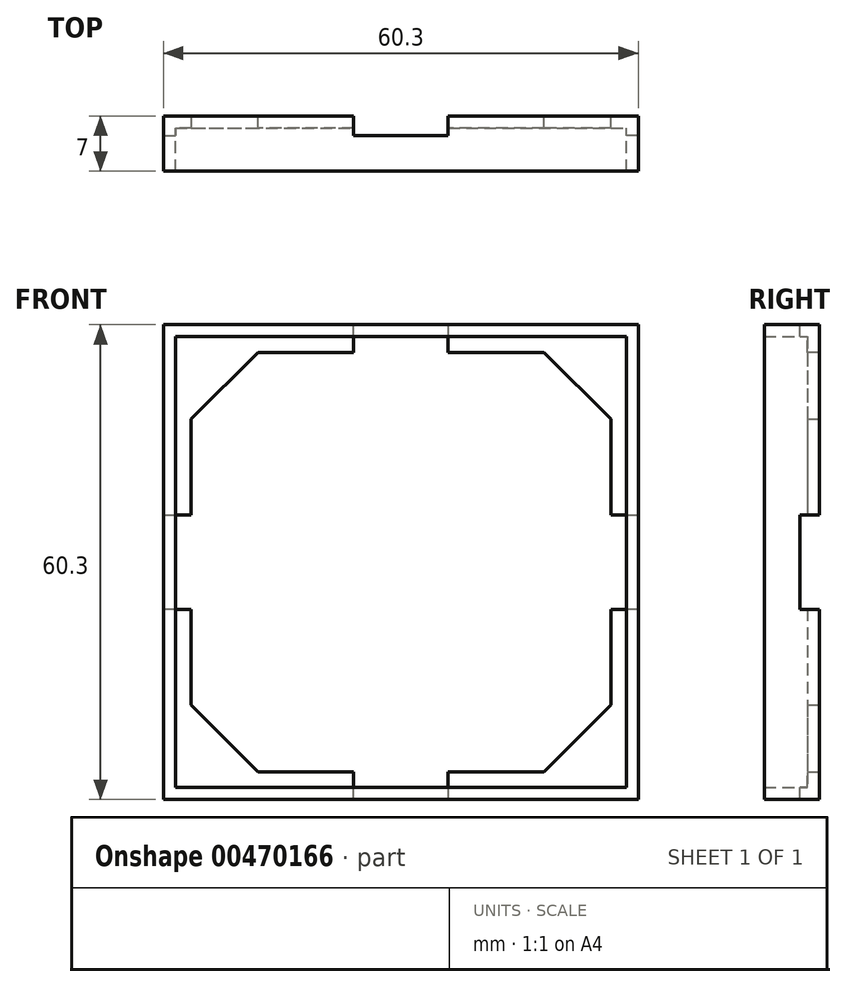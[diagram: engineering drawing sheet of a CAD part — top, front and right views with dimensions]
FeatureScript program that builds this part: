
annotation { "Feature Type Name" : "Feature", "Feature Type Description" : "" }
export const myFeature = defineFeature(function(context is Context, id is Id, definition is map)
    precondition{}
    {
        {
            var Q0;
            Q0=qCreatedBy(makeId("Front.planeOp"),FACE);
            var sketch = newSketch(context, id + "F0", { "sketchPlane" : qUnion([Q0])});
            skLineSegment(sketch, "E0.bottom", {"start": v(-28.65, 28.65) * mm, "end": v(28.65, 28.65) * mm});
            skLineSegment(sketch, "E0.top", {"start": v(-28.65, -28.65) * mm, "end": v(28.65, -28.65) * mm});
            skLineSegment(sketch, "E0.left", {"start": v(-28.65, 28.65) * mm, "end": v(-28.65, -28.65) * mm});
            skLineSegment(sketch, "E0.right", {"start": v(28.65, 28.65) * mm, "end": v(28.65, -28.65) * mm});
            skLineSegment(sketch, "E1", {"start": v(28.65, 28.65) * mm, "end": v(-28.65, -28.65) * mm, "construction": true});
            skLineSegment(sketch, "E2.bottom", {"start": v(18.16, 26.65) * mm, "end": v(-18.16, 26.65) * mm});
            skLineSegment(sketch, "E2.top", {"start": v(18.16, -26.65) * mm, "end": v(-18.16, -26.65) * mm});
            skLineSegment(sketch, "E2.left", {"start": v(26.65, 18.16) * mm, "end": v(26.65, -18.16) * mm});
            skLineSegment(sketch, "E2.right", {"start": v(-26.65, 18.16) * mm, "end": v(-26.65, -18.16) * mm});
            skLineSegment(sketch, "E3", {"start": v(18.16, 26.65) * mm, "end": v(26.65, 18.16) * mm});
            skPoint(sketch, "E4.orphan", {"position": v(26.65, 26.65) * mm});
            skLineSegment(sketch, "E5.1.0", {"start": v(-26.65, 18.16) * mm, "end": v(-18.16, 26.65) * mm});
            skLineSegment(sketch, "E5.2.0", {"start": v(-18.16, -26.65) * mm, "end": v(-26.65, -18.16) * mm});
            skLineSegment(sketch, "E5.3.0", {"start": v(26.65, -18.16) * mm, "end": v(18.16, -26.65) * mm});
            skPoint(sketch, "E5.center", {"position": v(0, 0) * mm});
            skSolve(sketch);
        }
        {
            var Q0;
            Q0=qSketchRegion(id+"F0",true);
            extrude(context, id + "F1", {"entities" : qUnion([Q0]), "depth" : 1.5 * mm});
        }
        {
            var Q0;
            Q0=qCreatedBy(makeId("Front.planeOp"),FACE);
            var sketch = newSketch(context, id + "F2", { "sketchPlane" : qUnion([Q0])});
            skLineSegment(sketch, "E6.0", {"start": v(-28.65, 30.15) * mm, "end": v(28.65, 30.15) * mm});
            skLineSegment(sketch, "E7.0", {"start": v(30.15, 28.65) * mm, "end": v(30.15, -28.65) * mm});
            skLineSegment(sketch, "E8.0", {"start": v(-28.65, -30.15) * mm, "end": v(28.65, -30.15) * mm});
            skLineSegment(sketch, "E9.0", {"start": v(-30.15, 28.65) * mm, "end": v(-30.15, -28.65) * mm});
            skLineSegment(sketch, "E10", {"start": v(-28.65, 30.15) * mm, "end": v(-30.15, 30.15) * mm});
            skLineSegment(sketch, "E11", {"start": v(-30.15, 30.15) * mm, "end": v(-30.15, 28.65) * mm});
            skLineSegment(sketch, "E12", {"start": v(-30.15, -28.65) * mm, "end": v(-30.15, -30.15) * mm});
            skLineSegment(sketch, "E13", {"start": v(-30.15, -30.15) * mm, "end": v(-28.65, -30.15) * mm});
            skLineSegment(sketch, "E14", {"start": v(30.15, -28.65) * mm, "end": v(30.15, -30.15) * mm});
            skLineSegment(sketch, "E15", {"start": v(30.15, -30.15) * mm, "end": v(28.65, -30.15) * mm});
            skLineSegment(sketch, "E16", {"start": v(28.65, 30.15) * mm, "end": v(30.15, 30.15) * mm});
            skPoint(sketch, "E16.endSnap0", {"position": v(30.15, 0) * mm});
            skLineSegment(sketch, "E17", {"start": v(30.15, 30.15) * mm, "end": v(30.15, 28.65) * mm});
            skLineSegment(sketch, "E18.0", {"start": v(-28.65, 28.65) * mm, "end": v(28.65, 28.65) * mm});
            skLineSegment(sketch, "E19.0", {"start": v(-28.65, 28.65) * mm, "end": v(-28.65, -28.65) * mm});
            skLineSegment(sketch, "E20.0", {"start": v(-28.65, -28.65) * mm, "end": v(28.65, -28.65) * mm});
            skLineSegment(sketch, "E21.0", {"start": v(28.65, 28.65) * mm, "end": v(28.65, -28.65) * mm});
            skSolve(sketch);
        }
        {
            var Q0;
            Q0=qSketchRegion(id+"F2",true);
            extrude(context, id + "F3", {"entities" : qUnion([Q0]), "operationType" : NewBodyOperationType.ADD, "depth" : 7 * mm});
        }
        {
            var Q0;
            Q0=qCreatedBy(makeId("Front.planeOp"),FACE);
            var sketch = newSketch(context, id + "F4", { "sketchPlane" : qUnion([Q0])});
            skLineSegment(sketch, "E22", {"start": v(25.58, 0) * mm, "end": v(25.58, 6) * mm});
            skLineSegment(sketch, "E23", {"start": v(25.58, 6) * mm, "end": v(33.95, 6) * mm});
            skLineSegment(sketch, "E24", {"start": v(33.95, 6) * mm, "end": v(33.95, -6) * mm});
            skLineSegment(sketch, "E25", {"start": v(33.95, -6) * mm, "end": v(25.58, -6) * mm});
            skLineSegment(sketch, "E26", {"start": v(25.58, -6) * mm, "end": v(25.58, 0) * mm});
            skLineSegment(sketch, "E27.1.0", {"start": v(-6, 25.58) * mm, "end": v(-6, 33.95) * mm});
            skLineSegment(sketch, "E27.1.1", {"start": v(-6, 33.95) * mm, "end": v(6, 33.95) * mm});
            skLineSegment(sketch, "E27.1.2", {"start": v(6, 25.58) * mm, "end": v(0, 25.58) * mm});
            skLineSegment(sketch, "E27.1.3", {"start": v(0, 25.58) * mm, "end": v(-6, 25.58) * mm});
            skLineSegment(sketch, "E27.1.4", {"start": v(6, 33.95) * mm, "end": v(6, 25.58) * mm});
            skLineSegment(sketch, "E27.2.0", {"start": v(-25.58, -6) * mm, "end": v(-33.95, -6) * mm});
            skLineSegment(sketch, "E27.2.1", {"start": v(-33.95, -6) * mm, "end": v(-33.95, 6) * mm});
            skLineSegment(sketch, "E27.2.2", {"start": v(-25.58, 6) * mm, "end": v(-25.58, 0) * mm});
            skLineSegment(sketch, "E27.2.3", {"start": v(-25.58, 0) * mm, "end": v(-25.58, -6) * mm});
            skLineSegment(sketch, "E27.2.4", {"start": v(-33.95, 6) * mm, "end": v(-25.58, 6) * mm});
            skLineSegment(sketch, "E27.3.0", {"start": v(6, -25.58) * mm, "end": v(6, -33.95) * mm});
            skLineSegment(sketch, "E27.3.1", {"start": v(6, -33.95) * mm, "end": v(-6, -33.95) * mm});
            skLineSegment(sketch, "E27.3.2", {"start": v(-6, -25.58) * mm, "end": v(0, -25.58) * mm});
            skLineSegment(sketch, "E27.3.3", {"start": v(0, -25.58) * mm, "end": v(6, -25.58) * mm});
            skLineSegment(sketch, "E27.3.4", {"start": v(-6, -33.95) * mm, "end": v(-6, -25.58) * mm});
            skPoint(sketch, "E27.center", {"position": v(0, 0) * mm});
            skSolve(sketch);
        }
        {
            var Q0;
            Q0=makeQuery(id+"F4.imprint","IMPRINT",FACE,{"disambiguationData":[TD([[makeQuery(id+"F4.imprint","IMPRINT",EDGE,{"derivedFrom":sQuery(id+"F4.wireOp",EDGE,"E22")}),-1.0]])]});
            var Q1;
            Q1=makeQuery(id+"F4.imprint","IMPRINT",FACE,{"disambiguationData":[TD([[makeQuery(id+"F4.imprint","IMPRINT",EDGE,{"derivedFrom":sQuery(id+"F4.wireOp",EDGE,"E27.1.0")}),-1.0]])]});
            var Q2;
            Q2=makeQuery(id+"F4.imprint","IMPRINT",FACE,{"disambiguationData":[TD([[makeQuery(id+"F4.imprint","IMPRINT",EDGE,{"derivedFrom":sQuery(id+"F4.wireOp",EDGE,"E27.2.0")}),-1.0]])]});
            var Q3;
            Q3=makeQuery(id+"F4.imprint","IMPRINT",FACE,{"disambiguationData":[TD([[makeQuery(id+"F4.imprint","IMPRINT",EDGE,{"derivedFrom":sQuery(id+"F4.wireOp",EDGE,"E27.3.0")}),-1.0]])]});
            extrude(context, id + "F5", {"entities" : qUnion([Q0, Q1, Q2, Q3]), "operationType" : NewBodyOperationType.REMOVE, "depth" : 2.5 * mm});
        }
    });
